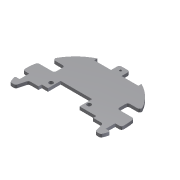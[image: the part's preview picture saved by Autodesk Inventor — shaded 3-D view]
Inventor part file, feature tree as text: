
AUTODESK INVENTOR PART (.ipt)
format: ipt  version: 2012 (Build 160160000, 160)  size: 184,320 bytes
history: native  units: mm
features: extrude x1, sketch x1
ambient origin geometry x8: Origin, YZ Plane, XZ Plane, XY Plane, X Axis, Y Axis, Z Axis, Center Point
feature tree (2):
  extrude  "Extrusion3"  Depth=30.0mm
  sketch  "Sketch1"  dims[d0=94.0mm d1=30.0mm d2=12.0mm d3=10.0mm d4=6.0mm d5=9.0mm d8=5.0mm d9=10.0mm d11=5.0mm d12=75.0deg d13=10.0mm d14=105.0deg d17=4.0mm d18=4.0mm d19=36.2mm d20=3.1mm d21=47.0mm d22=47.0mm d28=3.0mm d29=3.0mm d31=52.0mm d46=36.799497mm d51=2.0mm d58=12.0mm d59=3.0mm d60=3.0mm d88=47.0mm d89=42.0mm d92=3.0mm d93=10.0mm d94=5.0mm d95=2.0mm d96=4.0mm d97=3.0mm d98=0.0mm d99=2.0mm d101=9.0mm d103=9.0mm d104=47.0mm d105=47.0mm d106=47.0mm d107=47.0mm d108=10.0mm d109=30.0mm d110=10.0mm d111=10.0mm d112=30.0mm d113=2.0mm d114=41.0mm d115=41.0mm d116=1.0mm d117=2.0mm]
